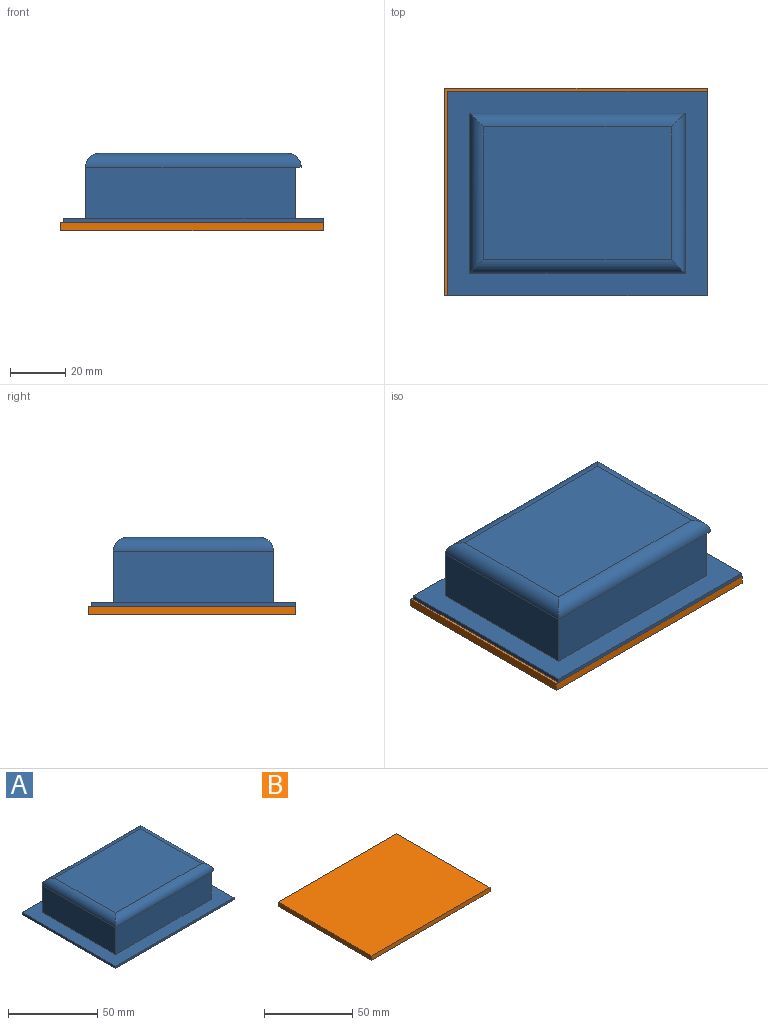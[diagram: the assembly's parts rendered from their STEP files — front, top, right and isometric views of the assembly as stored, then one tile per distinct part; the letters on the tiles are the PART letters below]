
ASSEMBLY  parts=2 mates=1
PART A: 26 faces, bbox 94x74x25 mm
  f0: plane 76x18.5mm, normal (0,1,0), area 1406mm2, adj f7,f10,f13,f25
  f1: plane 76x18.5mm, normal (0,-1,0), area 1406mm2, adj f7,f10,f12,f23
  f2: plane 54x1.5mm, normal (-1,0,0), area 81mm2, adj f7,f8,f16,f17
  f3: plane 74x1.5mm, normal (-1,0,0), area 111mm2, adj f4,f6,f7,f8
  f4: plane 94x1.5mm, normal (0,-1,0), area 141mm2, adj f3,f5,f7,f8
  f5: plane 74x1.5mm, normal (1,0,0), area 111mm2, adj f4,f6,f7,f8
  f6: plane 94x1.5mm, normal (0,1,0), area 141mm2, adj f3,f5,f7,f8
  f7: plane 94x74mm, normal (0,0,1), area 2548mm2, adj f0,f1,f2,f3,f4,f5,f6,f10
  f8: plane 94x74mm, normal (0,0,-1), area 2960mm2, adj f2,f3,f4,f5,f6,f16,f17,f18
  f9: plane 68x48mm, normal (0,0,1), area 3264mm2, adj f11,f12,f13,f14
  f10: plane 58x18.5mm, normal (-1,0,0), area 1073mm2, adj f0,f1,f7,f11
  f11: cylinder r=5mm len=58mm, axis (0,1,0), area 427mm2, adj f9,f10,f12,f13
  f12: cylinder r=5mm len=78mm, axis (-1,0,0), area 584.1mm2, adj f1,f9,f11,f14,f24
  f13: cylinder r=5mm len=78mm, axis (1,0,0), area 584.1mm2, adj f0,f9,f11,f14,f24
  f14: cylinder r=5mm len=58mm, axis (0,-1,0), area 427mm2, adj f9,f12,f13,f24
  f15: plane 68x48mm, normal (0,0,-1), area 3264mm2, adj f19,f20,f21,f22
  f16: plane 74x20mm, normal (0,-1,0), area 1480mm2, adj f2,f8,f18,f21,f25
  f17: plane 74x20mm, normal (0,1,0), area 1480mm2, adj f2,f8,f18,f20,f23
  f18: plane 54x20mm, normal (1,0,0), area 1080mm2, adj f8,f16,f17,f19
  f19: cylinder r=3mm len=54mm, axis (0,1,0), area 244.2mm2, adj f15,f18,f20,f21
  f20: cylinder r=3mm len=74mm, axis (-1,0,0), area 338.4mm2, adj f15,f17,f19,f22
  f21: cylinder r=3mm len=74mm, axis (1,0,0), area 338.4mm2, adj f15,f16,f19,f22
  f22: cylinder r=3mm len=54mm, axis (0,-1,0), area 244.2mm2, adj f15,f20,f21,f24
  f23: plane 18.5x2mm, normal (1,0,0), area 37mm2, adj f1,f7,f17,f24
  f24: plane 58x2mm, normal (0,0,-1), area 116mm2, adj f12,f13,f14,f22,f23,f25
  f25: plane 18.5x2mm, normal (1,0,0), area 37mm2, adj f0,f7,f16,f24
PART B: 6 faces, bbox 95x75x3 mm
  f0: plane 75x3mm, normal (-1,0,0), area 225mm2, adj f1,f3,f4,f5
  f1: plane 95x3mm, normal (0,-1,0), area 285mm2, adj f0,f2,f4,f5
  f2: plane 75x3mm, normal (1,0,0), area 225mm2, adj f1,f3,f4,f5
  f3: plane 95x3mm, normal (0,1,0), area 285mm2, adj f0,f2,f4,f5
  f4: plane 95x75mm, normal (0,0,1), area 7125mm2, adj f0,f1,f2,f3
  f5: plane 95x75mm, normal (0,0,-1), area 7125mm2, adj f0,f1,f2,f3
PLACE A t=(-33.1,-12.82,-8.35)mm
PLACE B t=(-34.1,-29.74,-11.35)mm
MATE fastened A.f8 <-> B.f4  axis (0,0,-1) through (44.02,-78.82,-8.35)mm
